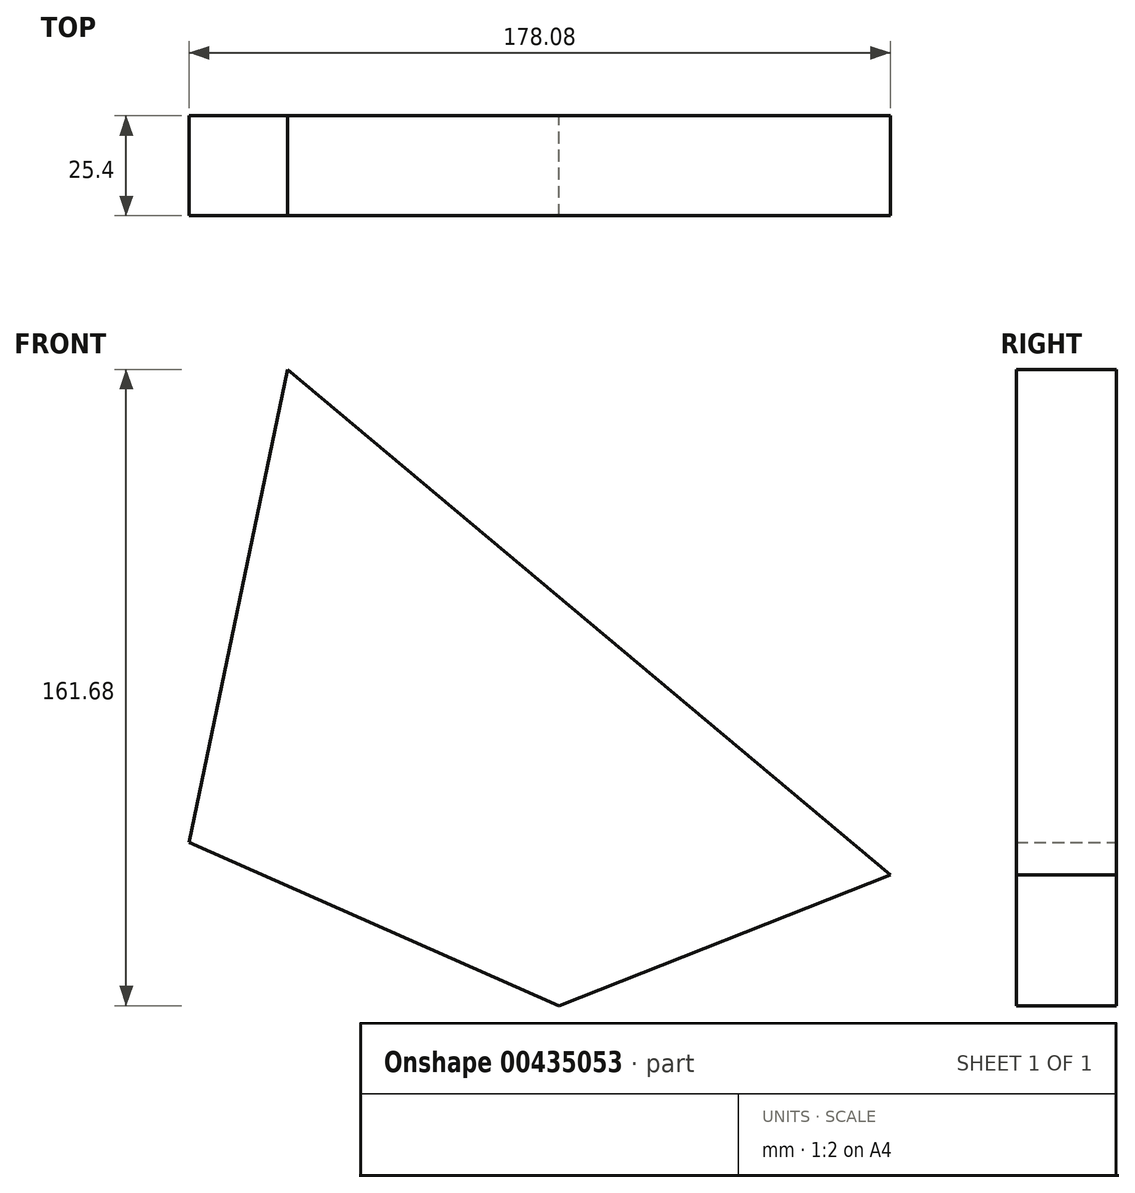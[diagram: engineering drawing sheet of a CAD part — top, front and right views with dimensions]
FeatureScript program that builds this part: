
annotation { "Feature Type Name" : "Feature", "Feature Type Description" : "" }
export const myFeature = defineFeature(function(context is Context, id is Id, definition is map)
    precondition{}
    {
        {
            var Q0;
            Q0=qCreatedBy(makeId("Front.planeOp"),FACE);
            var sketch = newSketch(context, id + "F0", { "sketchPlane" : qUnion([Q0])});
            skLineSegment(sketch, "E0", {"start": v(-25.02, -120.18) * mm, "end": v(68.96, -161.68) * mm});
            skLineSegment(sketch, "E1", {"start": v(68.96, -161.68) * mm, "end": v(153.06, -128.42) * mm});
            skLineSegment(sketch, "E2", {"start": v(153.06, -128.42) * mm, "end": v(0, 0) * mm});
            skLineSegment(sketch, "E3", {"start": v(-25.02, -120.18) * mm, "end": v(0, 0) * mm});
            skSolve(sketch);
        }
        {
            var Q0;
            Q0 = qSketchRegion(id + "F0", true);
            extrude(context, id + "F1", {"entities" : qUnion([Q0]), "depth" : 25.4 * mm});
        }
    });
